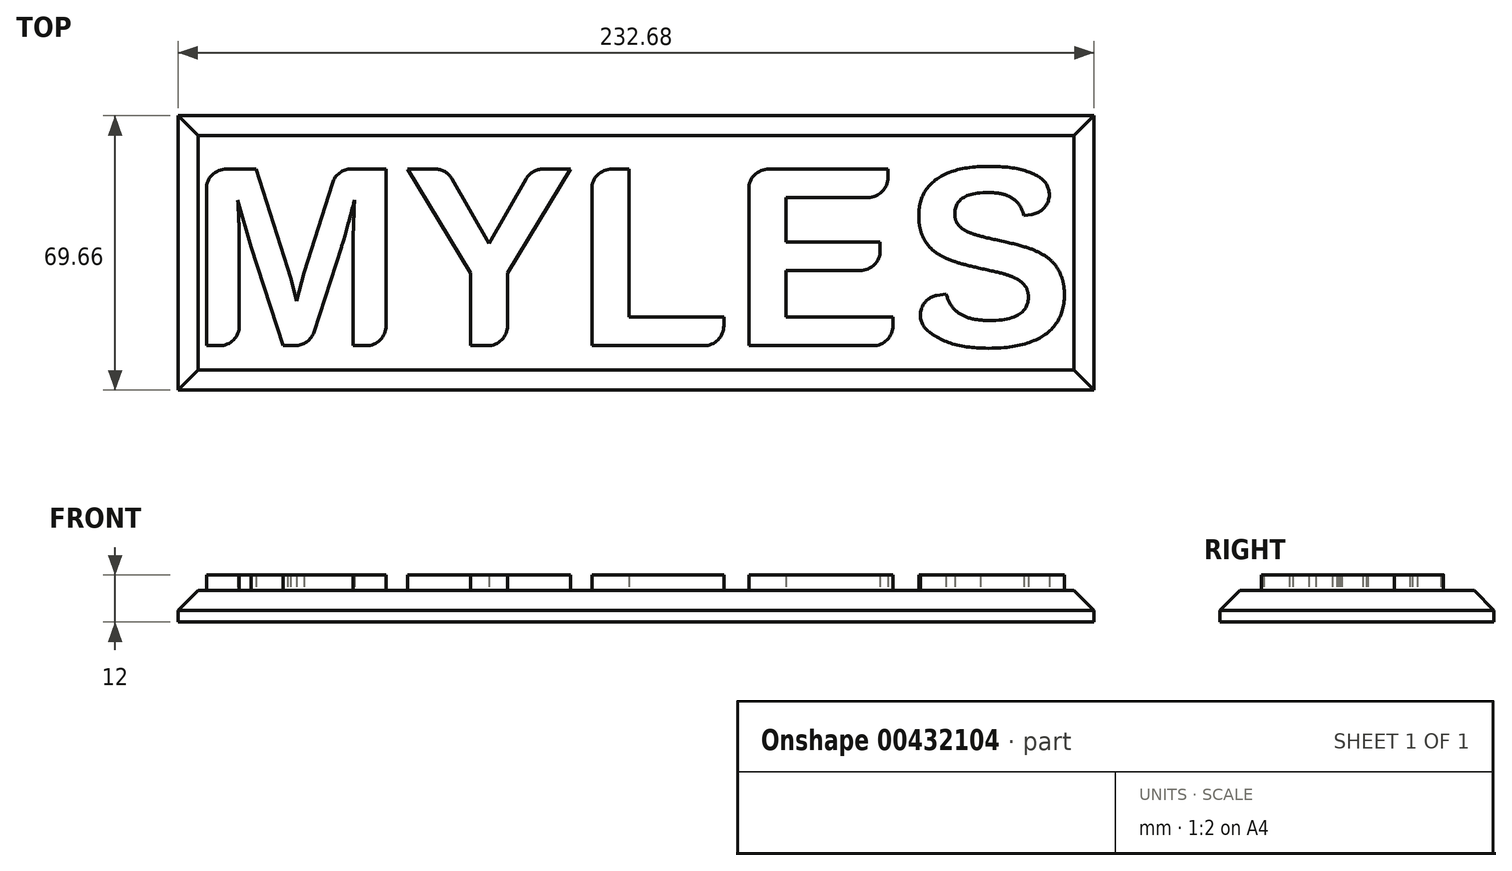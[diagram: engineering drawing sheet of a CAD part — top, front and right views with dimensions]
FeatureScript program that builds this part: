
annotation { "Feature Type Name" : "Feature", "Feature Type Description" : "" }
export const myFeature = defineFeature(function(context is Context, id is Id, definition is map)
    precondition{}
    {
        {
            var Q0;
            Q0=qCreatedBy(makeId("Top.planeOp"),FACE);
            var sketch = newSketch(context, id + "F0", { "sketchPlane" : qUnion([Q0])});
            skLineSegment(sketch, "E0.bottom", {"start": v(116.34, -34.83) * mm, "end": v(-116.34, -34.83) * mm});
            skLineSegment(sketch, "E0.top", {"start": v(116.34, 34.83) * mm, "end": v(-116.34, 34.83) * mm});
            skLineSegment(sketch, "E0.left", {"start": v(116.34, -34.83) * mm, "end": v(116.34, 34.83) * mm});
            skLineSegment(sketch, "E0.right", {"start": v(-116.34, -34.83) * mm, "end": v(-116.34, 34.83) * mm});
            skPoint(sketch, "E0.middle", {"position": v(0, 0) * mm});
            skText(sketch, "E1", { "text": "MYLES", "fontName": "Arimo-Bold.ttf"});
            const initialGuessF0  = {"E1": [-0.1135, -0.0236, 1, 0, 0.047]};
            skSetInitialGuess(sketch, initialGuessF0);
            skSolve(sketch);
        }
        {
            var Q0;
            Q0=makeQuery(id+"F0.imprint","IMPRINT",FACE,{"disambiguationData":[TD([[makeQuery(id+"F0.imprint","IMPRINT",EDGE,{"derivedFrom":sQuery(id+"F0.wireOp",EDGE,"E0.bottom")}),-1.0]])]});
            var Q1;
            Q1=makeQuery(id+"F0.imprint","IMPRINT",FACE,{"disambiguationData":[TD([[makeQuery(id+"F0.imprint","IMPRINT",EDGE,{"derivedFrom":sQuery(id+"F0.wireOp",EDGE,"E1.sketch_text.stroke-0")}),-1.0]])]});
            var Q2;
            Q2=makeQuery(id+"F0.imprint","IMPRINT",FACE,{"disambiguationData":[TD([[makeQuery(id+"F0.imprint","IMPRINT",EDGE,{"derivedFrom":sQuery(id+"F0.wireOp",EDGE,"E1.sketch_text.stroke-21")}),-1.0]])]});
            var Q3;
            Q3=makeQuery(id+"F0.imprint","IMPRINT",FACE,{"disambiguationData":[TD([[makeQuery(id+"F0.imprint","IMPRINT",EDGE,{"derivedFrom":sQuery(id+"F0.wireOp",EDGE,"E1.sketch_text.stroke-30")}),-1.0]])]});
            var Q4;
            Q4=makeQuery(id+"F0.imprint","IMPRINT",FACE,{"disambiguationData":[TD([[makeQuery(id+"F0.imprint","IMPRINT",EDGE,{"derivedFrom":sQuery(id+"F0.wireOp",EDGE,"E1.sketch_text.stroke-36")}),-1.0]])]});
            var Q5;
            Q5=makeQuery(id+"F0.imprint","IMPRINT",FACE,{"disambiguationData":[TD([[makeQuery(id+"F0.imprint","IMPRINT",EDGE,{"derivedFrom":sQuery(id+"F0.wireOp",EDGE,"E1.sketch_text.stroke-48")}),-1.0]])]});
            extrude(context, id + "F1", {"entities" : qUnion([Q0, Q1, Q2, Q3, Q4, Q5]), "depth" : 8 * mm});
        }
        {
            var Q0;
            Q0=makeQuery(id+"F0.imprint","IMPRINT",FACE,{"disambiguationData":[TD([[makeQuery(id+"F0.imprint","IMPRINT",EDGE,{"derivedFrom":sQuery(id+"F0.wireOp",EDGE,"E1.sketch_text.stroke-21")}),-1.0]])]});
            var Q1;
            Q1=makeQuery(id+"F0.imprint","IMPRINT",FACE,{"disambiguationData":[TD([[makeQuery(id+"F0.imprint","IMPRINT",EDGE,{"derivedFrom":sQuery(id+"F0.wireOp",EDGE,"E1.sketch_text.stroke-0")}),-1.0]])]});
            var Q2;
            Q2=makeQuery(id+"F0.imprint","IMPRINT",FACE,{"disambiguationData":[TD([[makeQuery(id+"F0.imprint","IMPRINT",EDGE,{"derivedFrom":sQuery(id+"F0.wireOp",EDGE,"E1.sketch_text.stroke-30")}),-1.0]])]});
            var Q3;
            Q3=makeQuery(id+"F0.imprint","IMPRINT",FACE,{"disambiguationData":[TD([[makeQuery(id+"F0.imprint","IMPRINT",EDGE,{"derivedFrom":sQuery(id+"F0.wireOp",EDGE,"E1.sketch_text.stroke-36")}),-1.0]])]});
            var Q4;
            Q4=makeQuery(id+"F0.imprint","IMPRINT",FACE,{"disambiguationData":[TD([[makeQuery(id+"F0.imprint","IMPRINT",EDGE,{"derivedFrom":sQuery(id+"F0.wireOp",EDGE,"E1.sketch_text.stroke-48")}),-1.0]])]});
            extrude(context, id + "F2", {"entities" : qUnion([Q0, Q1, Q2, Q3, Q4]), "operationType" : NewBodyOperationType.ADD, "depth" : 12 * mm});
        }
        {
            var Q0;
            Q0=makeQuery(id+"F1.opExtrude","CAP_EDGE",EDGE,{"disambiguationData":[OSD([sQuery(id+"F0.wireOp",EDGE,"E0.top")])],"isStart":false});
            var Q1;
            Q1=makeQuery(id+"F1.opExtrude","CAP_EDGE",EDGE,{"disambiguationData":[OSD([sQuery(id+"F0.wireOp",EDGE,"E0.right")])],"isStart":false});
            var Q2;
            Q2=makeQuery(id+"F1.opExtrude","CAP_EDGE",EDGE,{"disambiguationData":[OSD([sQuery(id+"F0.wireOp",EDGE,"E0.bottom")])],"isStart":false});
            var Q3;
            Q3=makeQuery(id+"F1.opExtrude","CAP_EDGE",EDGE,{"disambiguationData":[OSD([sQuery(id+"F0.wireOp",EDGE,"E0.left")])],"isStart":false});
            chamfer(context, id + "F3", {"entities" : qUnion([Q0, Q1, Q2, Q3]), "width" : 5.08 * mm, "tangentPropagation" : true});
        }
        {
            var Q0;
            Q0=makeQuery(id+"F2.opExtrude","SWEPT_EDGE",EDGE,{"disambiguationData":[OSD([sQuery(id+"F0.wireOp",EDGE,"E1.sketch_text.stroke-30"),sQuery(id+"F0.wireOp",EDGE,"E1.sketch_text.stroke-31")])]});
            var Q1;
            Q1=makeQuery(id+"F2.opExtrude","SWEPT_EDGE",EDGE,{"disambiguationData":[OSD([sQuery(id+"F0.wireOp",EDGE,"E1.sketch_text.stroke-27"),sQuery(id+"F0.wireOp",EDGE,"E1.sketch_text.stroke-28")])]});
            var Q2;
            Q2=makeQuery(id+"F2.opExtrude","SWEPT_EDGE",EDGE,{"disambiguationData":[OSD([sQuery(id+"F0.wireOp",EDGE,"E1.sketch_text.stroke-25"),sQuery(id+"F0.wireOp",EDGE,"E1.sketch_text.stroke-26")])]});
            var Q3;
            Q3=makeQuery(id+"F2.opExtrude","SWEPT_EDGE",EDGE,{"disambiguationData":[OSD([sQuery(id+"F0.wireOp",EDGE,"E1.sketch_text.stroke-34"),sQuery(id+"F0.wireOp",EDGE,"E1.sketch_text.stroke-35")])]});
            var Q4;
            Q4=makeQuery(id+"F2.opExtrude","SWEPT_EDGE",EDGE,{"disambiguationData":[OSD([sQuery(id+"F0.wireOp",EDGE,"E1.sketch_text.stroke-17"),sQuery(id+"F0.wireOp",EDGE,"E1.sketch_text.stroke-18")])]});
            var Q5;
            Q5=makeQuery(id+"F2.opExtrude","SWEPT_EDGE",EDGE,{"disambiguationData":[OSD([sQuery(id+"F0.wireOp",EDGE,"E1.sketch_text.stroke-11"),sQuery(id+"F0.wireOp",EDGE,"E1.sketch_text.stroke-12")])]});
            var Q6;
            Q6=makeQuery(id+"F2.opExtrude","SWEPT_EDGE",EDGE,{"disambiguationData":[OSD([sQuery(id+"F0.wireOp",EDGE,"E1.sketch_text.stroke-19"),sQuery(id+"F0.wireOp",EDGE,"E1.sketch_text.stroke-20")])]});
            var Q7;
            Q7=makeQuery(id+"F2.opExtrude","SWEPT_EDGE",EDGE,{"disambiguationData":[OSD([sQuery(id+"F0.wireOp",EDGE,"E1.sketch_text.stroke-9"),sQuery(id+"F0.wireOp",EDGE,"E1.sketch_text.stroke-10")])]});
            var Q8;
            Q8=makeQuery(id+"F2.opExtrude","SWEPT_EDGE",EDGE,{"disambiguationData":[OSD([sQuery(id+"F0.wireOp",EDGE,"E1.sketch_text.stroke-4"),sQuery(id+"F0.wireOp",EDGE,"E1.sketch_text.stroke-5")])]});
            var Q9;
            Q9=makeQuery(id+"F2.opExtrude","SWEPT_EDGE",EDGE,{"disambiguationData":[OSD([sQuery(id+"F0.wireOp",EDGE,"E1.sketch_text.stroke-21"),sQuery(id+"F0.wireOp",EDGE,"E1.sketch_text.stroke-22")])]});
            var Q10;
            Q10=makeQuery(id+"F2.opExtrude","SWEPT_EDGE",EDGE,{"disambiguationData":[OSD([sQuery(id+"F0.wireOp",EDGE,"E1.sketch_text.stroke-46"),sQuery(id+"F0.wireOp",EDGE,"E1.sketch_text.stroke-47")])]});
            var Q11;
            Q11=makeQuery(id+"F2.opExtrude","SWEPT_EDGE",EDGE,{"disambiguationData":[OSD([sQuery(id+"F0.wireOp",EDGE,"E1.sketch_text.stroke-42"),sQuery(id+"F0.wireOp",EDGE,"E1.sketch_text.stroke-43")])]});
            var Q12;
            Q12=makeQuery(id+"F2.opExtrude","SWEPT_EDGE",EDGE,{"disambiguationData":[OSD([sQuery(id+"F0.wireOp",EDGE,"E1.sketch_text.stroke-38"),sQuery(id+"F0.wireOp",EDGE,"E1.sketch_text.stroke-39")])]});
            var Q13;
            Q13=makeQuery(id+"F2.opExtrude","SWEPT_EDGE",EDGE,{"disambiguationData":[OSD([sQuery(id+"F0.wireOp",EDGE,"E1.sketch_text.stroke-36"),sQuery(id+"F0.wireOp",EDGE,"E1.sketch_text.stroke-37")])]});
            var Q14;
            Q14=makeQuery(id+"F2.opExtrude","SWEPT_EDGE",EDGE,{"disambiguationData":[OSD([sQuery(id+"F0.wireOp",EDGE,"E1.sketch_text.stroke-51"),sQuery(id+"F0.wireOp",EDGE,"E1.sketch_text.stroke-52")])]});
            var Q15;
            Q15=makeQuery(id+"F2.opExtrude","SWEPT_EDGE",EDGE,{"disambiguationData":[OSD([sQuery(id+"F0.wireOp",EDGE,"E1.sketch_text.stroke-67"),sQuery(id+"F0.wireOp",EDGE,"E1.sketch_text.stroke-68")])]});
            fillet(context, id + "F4", {"entities" : qUnion([Q0, Q1, Q2, Q3, Q4, Q5, Q6, Q7, Q8, Q9, Q10, Q11, Q12, Q13, Q14, Q15]), "radius" : 5.08 * mm, "tangentPropagation" : true, "allowEdgeOverflow" : false});
        }
    });
